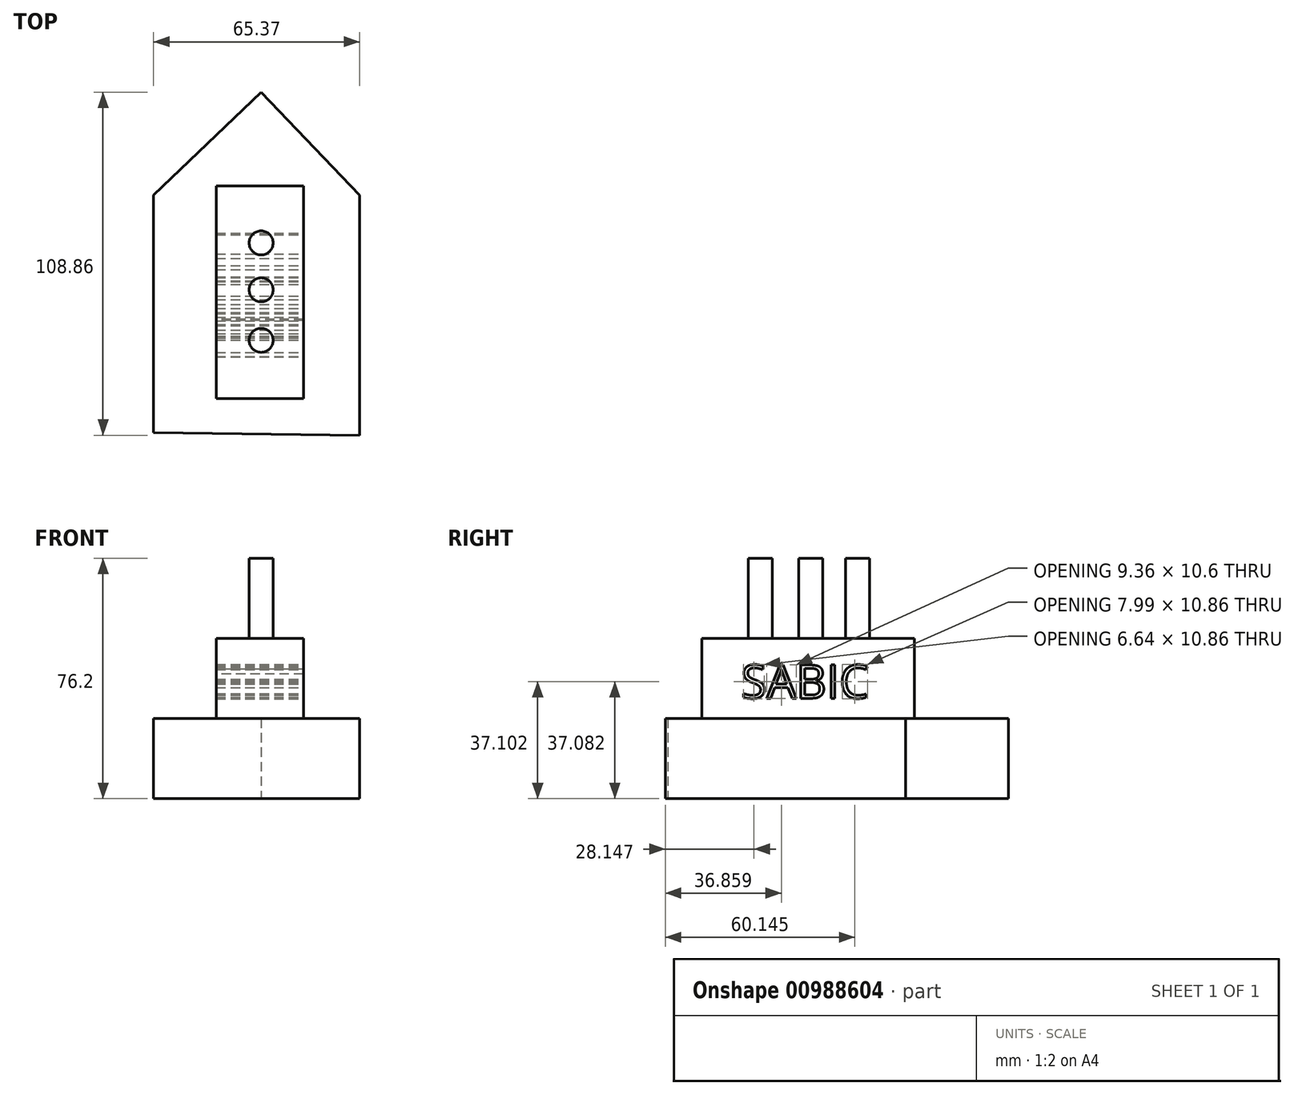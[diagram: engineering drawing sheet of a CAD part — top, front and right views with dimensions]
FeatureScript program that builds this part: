
annotation { "Feature Type Name" : "Feature", "Feature Type Description" : "" }
export const myFeature = defineFeature(function(context is Context, id is Id, definition is map)
    precondition{}
    {
        {
            var Q0;
            Q0=qCreatedBy(makeId("Top.planeOp"),FACE);
            var sketch = newSketch(context, id + "F0", { "sketchPlane" : qUnion([Q0])});
            skLineSegment(sketch, "E0", {"start": v(0, 76.4) * mm, "end": v(-34.12, 43.75) * mm});
            skLineSegment(sketch, "E1", {"start": v(0, 76.4) * mm, "end": v(31.25, 43.75) * mm});
            skLineSegment(sketch, "E2", {"start": v(-34.12, 43.75) * mm, "end": v(-34.12, -31.61) * mm});
            skLineSegment(sketch, "E3", {"start": v(31.25, 43.75) * mm, "end": v(31.25, -32.45) * mm});
            skLineSegment(sketch, "E4", {"start": v(31.25, -32.45) * mm, "end": v(-34.12, -31.61) * mm});
            skSolve(sketch);
        }
        {
            var Q0;
            Q0 = qSketchRegion(id + "F0", true);
            extrude(context, id + "F1", {"entities" : qUnion([Q0]), "depth" : 25.4 * mm, "offsetDistance" : 25.4 * mm});
        }
        {
            var Q0;
            Q0=makeQuery(id+"F1.opExtrude","CAP_FACE",FACE,{"disambiguationData":[OSD([sQuery(id+"F0.wireOp",EDGE,"E0"),sQuery(id+"F0.wireOp",EDGE,"E1"),sQuery(id+"F0.wireOp",EDGE,"E2"),sQuery(id+"F0.wireOp",EDGE,"E3"),sQuery(id+"F0.wireOp",EDGE,"E4")])],"isStart":false});
            var sketch = newSketch(context, id + "F2", { "sketchPlane" : qUnion([Q0])});
            skLineSegment(sketch, "E5.bottom", {"start": v(13.4, 46.65) * mm, "end": v(-14.27, 46.65) * mm});
            skLineSegment(sketch, "E5.top", {"start": v(13.4, -20.79) * mm, "end": v(-14.27, -20.79) * mm});
            skLineSegment(sketch, "E5.left", {"start": v(13.4, 46.65) * mm, "end": v(13.4, -20.79) * mm});
            skLineSegment(sketch, "E5.right", {"start": v(-14.27, 46.65) * mm, "end": v(-14.27, -20.79) * mm});
            skSolve(sketch);
        }
        {
            var Q0;
            Q0 = qSketchRegion(id + "F2", true);
            extrude(context, id + "F3", {"entities" : qUnion([Q0]), "operationType" : NewBodyOperationType.ADD, "depth" : 25.4 * mm, "offsetDistance" : 25.4 * mm});
        }
        {
            var Q0;
            Q0=makeQuery(id+"F3.opExtrude","CAP_FACE",FACE,{"disambiguationData":[OSD([sQuery(id+"F2.wireOp",EDGE,"E5.bottom"),sQuery(id+"F2.wireOp",EDGE,"E5.top"),sQuery(id+"F2.wireOp",EDGE,"E5.left"),sQuery(id+"F2.wireOp",EDGE,"E5.right")])],"isStart":false});
            var sketch = newSketch(context, id + "F4", { "sketchPlane" : qUnion([Q0])});
            skCircle(sketch, "E6", {"center": v(0, 28.57) * mm, "radius": 3.81 * mm});
            skCircle(sketch, "E7", {"center": v(0, 13.7) * mm, "radius": 3.81 * mm});
            skCircle(sketch, "E8", {"center": v(0, -2.32) * mm, "radius": 3.81 * mm});
            skSolve(sketch);
        }
        {
            var Q0;
            Q0 = qSketchRegion(id + "F4", true);
            extrude(context, id + "F5", {"entities" : qUnion([Q0]), "operationType" : NewBodyOperationType.ADD, "depth" : 25.4 * mm, "offsetDistance" : 25.4 * mm});
        }
        {
            var Q0;
            Q0=makeQuery(id+"F3.opExtrude","SWEPT_FACE",FACE,{"disambiguationData":[OSD([sQuery(id+"F2.wireOp",EDGE,"E5.left")])]});
            var sketch = newSketch(context, id + "F6", { "sketchPlane" : qUnion([Q0])});
            skText(sketch, "E9", { "text": "SABIC", "fontName": "OpenSans-Regular.ttf"});
            const initialGuessF6  = {"E9": [-0.00839, 0.0318, 1, 0, 0.01065]};
            skSetInitialGuess(sketch, initialGuessF6);
            skSolve(sketch);
        }
        {
            var Q0;
            Q0 = qSketchRegion(id + "F6", true);
            extrude(context, id + "F7", {"entities" : qUnion([Q0]), "operationType" : NewBodyOperationType.REMOVE, "oppositeDirection" : true, "depth" : 63.5 * mm, "offsetDistance" : 25.4 * mm});
        }
    });
